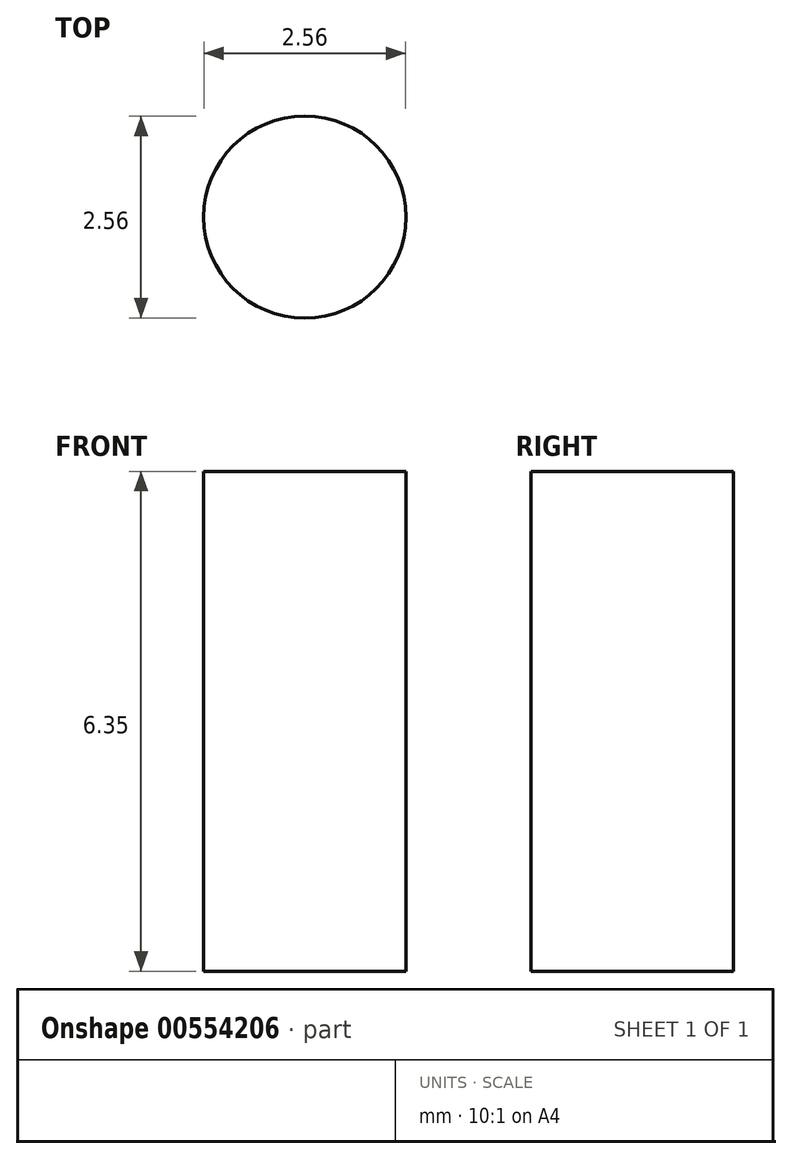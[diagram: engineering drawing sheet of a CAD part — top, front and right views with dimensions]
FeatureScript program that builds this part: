
annotation { "Feature Type Name" : "Feature", "Feature Type Description" : "" }
export const myFeature = defineFeature(function(context is Context, id is Id, definition is map)
    precondition{}
    {
        {
            var Q0;
            Q0=qCreatedBy(makeId("Top.planeOp"),FACE);
            var sketch = newSketch(context, id + "F0", { "sketchPlane" : qUnion([Q0])});
            skCircle(sketch, "E0", {"center": v(0, 0) * mm, "radius": 1.28 * mm});
            skSolve(sketch);
        }
        {
            var Q0;
            Q0=sQuery(id+"F0.wireOp",EDGE,"E0");
            extrude(context, id + "F1", {"bodyType" : ToolBodyType.SURFACE, "surfaceEntities" : qUnion([Q0]), "depth" : 6.35 * mm, "offsetDistance" : 25.4 * mm});
        }
    });
